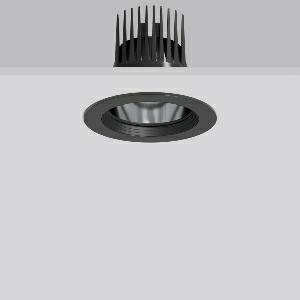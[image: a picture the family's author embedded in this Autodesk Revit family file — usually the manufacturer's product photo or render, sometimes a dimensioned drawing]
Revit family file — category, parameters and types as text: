
# Revit family: heledon_maxi_e_901758_003_1_76_2723
name_source: partatom
category: Lighting Fixtures
units: mm (PartAtom-declared; Revit-internal decimal feet)

## family parameters
Cut with Voids When Loaded = No
Host = Face
Light Source = No
Part Type = Normal
Room Calculation Point = No
Round Connector Dimension = Use Diameter
Shared = No

## types (1)
- HELEDON maxi E (1 x LED Modul 940, 3500 lm, 4000)
    Apparent Load = 25 VA
    Approval mark = CE
    CIE Flux Codes = 100 100 100 100 100
    Color Rendering = 92
    Color Temperature = 4000
    Default Elevation = 1800 mm
    Description = Series: HELEDON maxi
Round recessed downlight. Housing: die-cast aluminium, powder-coated. Black plastic ring and recessed LED to prevent glare from the side. Optical assembly with reflector made of MIRO-Silver with 98% total light reflection for outstanding efficiency - can be changed without tools. Best colour rendering index Ra>90. Suitable for Recessed ceiling mounting. Installation without tools thanks to spring fastening system. Including separate LED converter with connecting cable 600 mm.High quality converter without flickering and stroboscopic effect. Through-wiring box (5 pole) available as accessory. The following accessories can be mounted without use of tools: interchangeable lenses, decorative glasses, honeycomb louvre, clear and frosted diffusers, white interchangeable plastic ring. 
Colour: deep black, matt (RAL 9005)
Diameter: 162 mm
Height: 3 mm
Cut-out diameter: 152 mm
Recess height: 200 mm
Luminaire: recess height: 135 mm
Lamp: LED
Socket: without socket
Colour temperature: 4000K
Colour rendering index (CRI): 92
System power: 25 W
Rated luminous flux: 3500 lm
Luminous efficiency: 140 lm/W
Control gear: Converter, dimmable, DALI
Protection class: II
Type of protection: IP 20
    Height = 0 mm  [stored 0 ft]
    Lamp = 1 x LED Modul 940
    Lamp Light Flux = 3500 lm
    Lamp count = 1
    Length = 162 mm
    Lifetime = 50000 h
    Luminous efficacy = 140 lm/W
    Manufacturer = RZB
    ModVariant = No
    Model = 901758.003.1.76
    Mounting Place = Ceiling
    Mounting Type = Recessed
    Number of Poles = 1
    OnlyDefault = Yes
    Power Factor = 1
    Product Name = HELEDON maxi E
    Product group = Recessed downlights
    ProductGroupID = 402
    Protection Class = Protection class II
    Protection Degree = IP 20
    RLX_Detail_Level = 1
    RLX_Emergency_Light_Flux = 0 lm
    RLX_Emergency_Type = 0
    RLX_Emergency_Type_DB = No
    RlxData = <blob elided: 120541 chars, md5=16569d65>
    Socket = socket
    Standby Power = 0 W
    System Light Flux = 3500 lm
    System Power = 25 W
    Type Comments = Product without accessories
    Type Image = 901662.003.jpg
    URL = http://relux.com
    VarID = ---
    Voltage = 230 V
    Voltage Range = 220-240 V
    Weight = 0.00 kg
    Width = 0 mm  [stored 0 ft]

note: [stored X ft] marks values corroborated as IEEE doubles in the binary element streams (Revit-internal decimal feet)

## geometry (parser evidence)
native form markers: Blend x4, Sweep x11
no freeform markers — native parametric forms only
